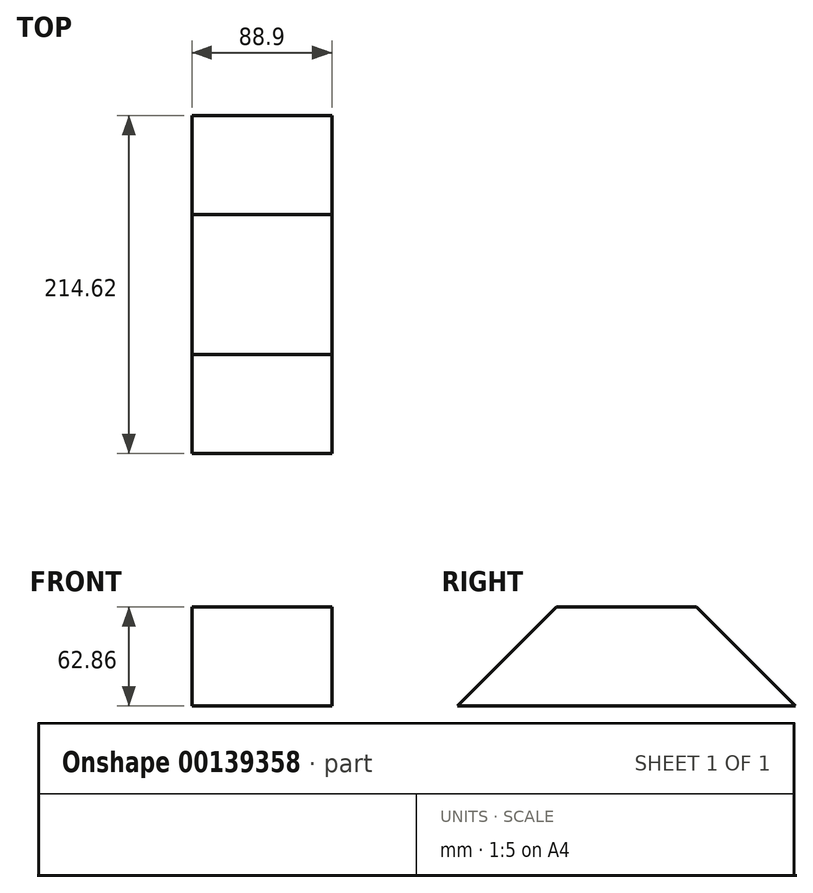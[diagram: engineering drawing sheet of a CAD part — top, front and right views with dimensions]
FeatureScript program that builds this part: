
annotation { "Feature Type Name" : "Feature", "Feature Type Description" : "" }
export const myFeature = defineFeature(function(context is Context, id is Id, definition is map)
    precondition{}
    {
        {
            var Q0;
            Q0=qCreatedBy(makeId("Right.planeOp"),FACE);
            var sketch = newSketch(context, id + "F0", { "sketchPlane" : qUnion([Q0])});
            skLineSegment(sketch, "E0", {"start": v(-47.63, 62.86) * mm, "end": v(-110.5, 0) * mm});
            skLineSegment(sketch, "E1", {"start": v(-110.5, 0) * mm, "end": v(-110.5, 0) * mm});
            skLineSegment(sketch, "E2", {"start": v(41.27, 62.86) * mm, "end": v(-47.63, 62.86) * mm});
            skLineSegment(sketch, "E3", {"start": v(104.13, 0) * mm, "end": v(41.27, 62.86) * mm});
            skLineSegment(sketch, "E4", {"start": v(-110.5, 0) * mm, "end": v(104.13, 0) * mm});
            skSolve(sketch);
        }
        {
            var Q0;
            Q0=makeQuery(id+"F0.imprint","IMPRINT",FACE,{"disambiguationData":[TD([[makeQuery(id+"F0.imprint","IMPRINT",EDGE,{"derivedFrom":sQuery(id+"F0.wireOp",EDGE,"E0")}),1.0]])]});
            extrude(context, id + "F1", {"entities" : qUnion([Q0]), "depth" : 88.9 * mm});
        }
    });
